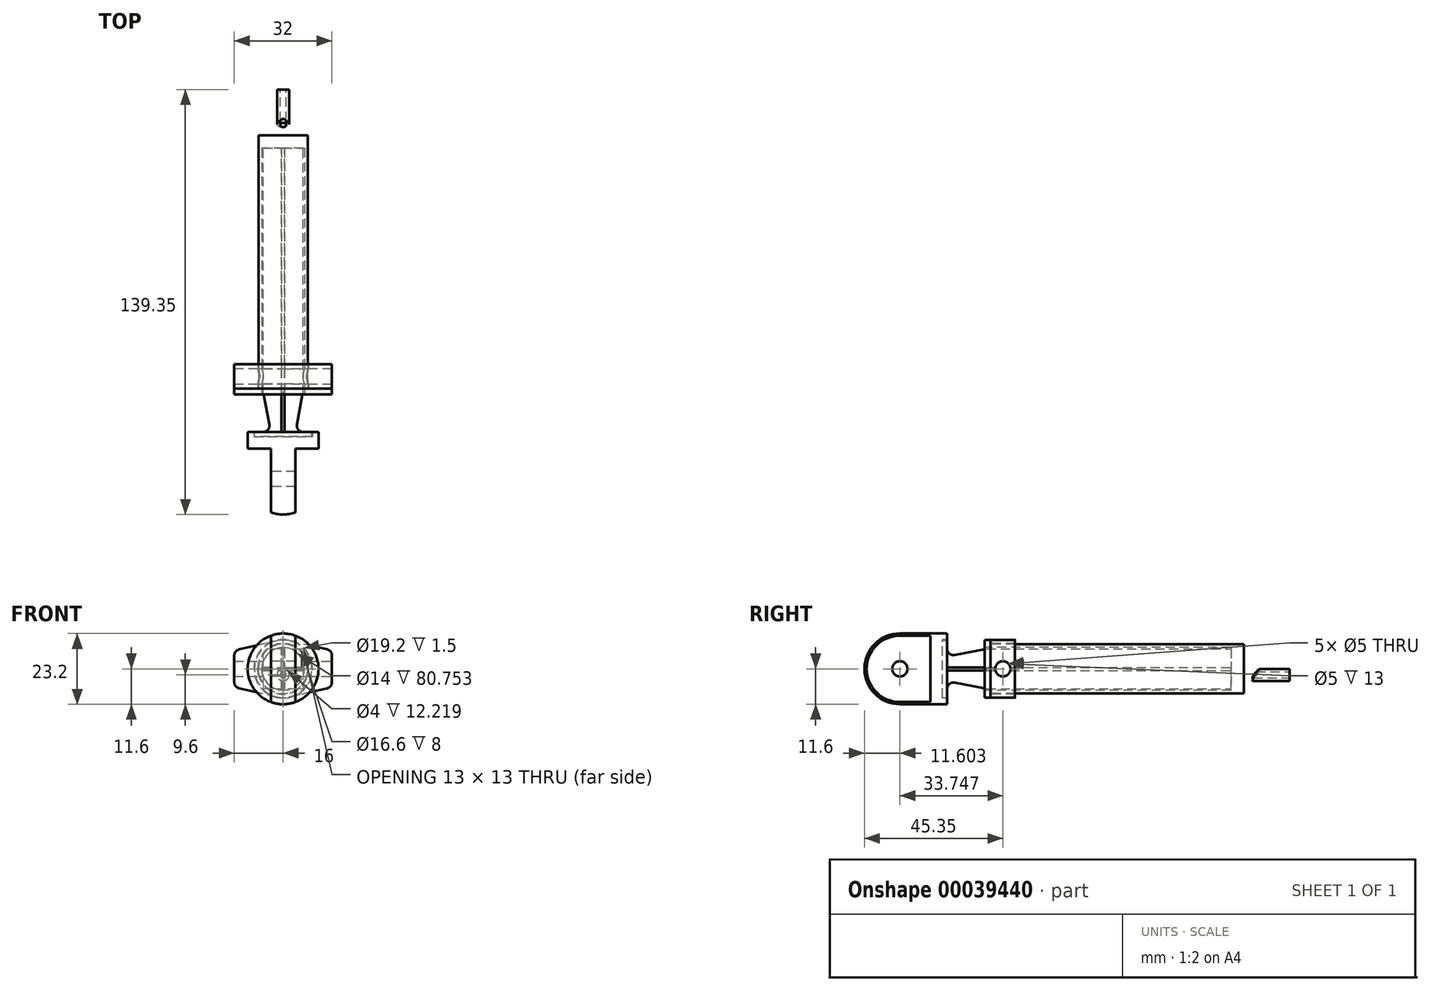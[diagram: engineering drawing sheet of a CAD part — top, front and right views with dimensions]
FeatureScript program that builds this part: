
annotation { "Feature Type Name" : "Feature", "Feature Type Description" : "" }
export const myFeature = defineFeature(function(context is Context, id is Id, definition is map)
    precondition{}
    {
        {
            var Q0;
            Q0=qCreatedBy(makeId("Front.planeOp"),FACE);
            var sketch = newSketch(context, id + "F0", { "sketchPlane" : qUnion([Q0])});
            skCircle(sketch, "E0", {"center": v(0, 0) * mm, "radius": 7 * mm});
            skArc(sketch, "E1", {"start": v(-2.17, -9.25) * mm, "mid": v(0, -9.5) * mm, "end": v(2.17, -9.25) * mm});
            skLineSegment(sketch, "E2", {"start": v(-2.17, -9.25) * mm, "end": v(-14.46, -6.36) * mm});
            skLineSegment(sketch, "E3", {"start": v(-16, -4.42) * mm, "end": v(-16, 4.42) * mm});
            skLineSegment(sketch, "E4", {"start": v(-14.46, 6.36) * mm, "end": v(-2.17, 9.25) * mm});
            skLineSegment(sketch, "E5", {"start": v(2.17, 9.25) * mm, "end": v(14.46, 6.36) * mm});
            skLineSegment(sketch, "E6", {"start": v(16, 4.42) * mm, "end": v(16, -4.42) * mm});
            skLineSegment(sketch, "E7", {"start": v(14.46, -6.36) * mm, "end": v(2.17, -9.25) * mm});
            skLineSegment(sketch, "E8", {"start": v(-16, 0) * mm, "end": v(16, 0) * mm, "construction": true});
            skArc(sketch, "E9.trimOffspring", {"start": v(2.17, 9.25) * mm, "mid": v(0, 9.5) * mm, "end": v(-2.17, 9.25) * mm});
            skPoint(sketch, "E10.visualSharp", {"position": v(-16, 6) * mm});
            skArc(sketch, "E10.filletArc", {"start": v(-14.46, 6.36) * mm, "mid": v(-15.57, 5.66) * mm, "end": v(-16, 4.42) * mm});
            skPoint(sketch, "E11.visualSharp", {"position": v(-16, -6) * mm});
            skArc(sketch, "E11.filletArc", {"start": v(-16, -4.42) * mm, "mid": v(-15.57, -5.66) * mm, "end": v(-14.46, -6.36) * mm});
            skPoint(sketch, "E12.visualSharp", {"position": v(16, -6) * mm});
            skArc(sketch, "E12.filletArc", {"start": v(14.46, -6.36) * mm, "mid": v(15.57, -5.66) * mm, "end": v(16, -4.42) * mm});
            skPoint(sketch, "E13.visualSharp", {"position": v(16, 6) * mm});
            skArc(sketch, "E13.filletArc", {"start": v(16, 4.42) * mm, "mid": v(15.57, 5.66) * mm, "end": v(14.46, 6.36) * mm});
            skSolve(sketch);
        }
        {
            var Q0;
            Q0=makeQuery(id+"F0.imprint","IMPRINT",FACE,{"disambiguationData":[TD([[makeQuery(id+"F0.imprint","IMPRINT",EDGE,{"derivedFrom":sQuery(id+"F0.wireOp",EDGE,"E0")}),-1.0]])]});
            extrude(context, id + "F1", {"entities" : qUnion([Q0]), "oppositeDirection" : true, "depth" : 2 * mm});
        }
        {
            var Q0;
            Q0=makeQuery(id+"F1.opExtrude","CAP_FACE",FACE,{"disambiguationData":[OSD([sQuery(id+"F0.wireOp",EDGE,"E0"),sQuery(id+"F0.wireOp",EDGE,"E1"),sQuery(id+"F0.wireOp",EDGE,"E2"),sQuery(id+"F0.wireOp",EDGE,"E3"),sQuery(id+"F0.wireOp",EDGE,"E4"),sQuery(id+"F0.wireOp",EDGE,"E5"),sQuery(id+"F0.wireOp",EDGE,"E6"),sQuery(id+"F0.wireOp",EDGE,"E7"),sQuery(id+"F0.wireOp",EDGE,"E9.trimOffspring"),sQuery(id+"F0.wireOp",EDGE,"E10.filletArc"),sQuery(id+"F0.wireOp",EDGE,"E11.filletArc"),sQuery(id+"F0.wireOp",EDGE,"E12.filletArc"),sQuery(id+"F0.wireOp",EDGE,"E13.filletArc")])],"isStart":false});
            var sketch = newSketch(context, id + "F2", { "sketchPlane" : qUnion([Q0])});
            skCircle(sketch, "E14.0", {"center": v(0, 0) * mm, "radius": 7 * mm});
            skCircle(sketch, "E15", {"center": v(0, 0) * mm, "radius": 8.1 * mm});
            skSolve(sketch);
        }
        {
            var Q0;
            Q0=makeQuery(id+"F2.imprint","IMPRINT",FACE,{"disambiguationData":[TD([[makeQuery(id+"F2.imprint","IMPRINT",EDGE,{"derivedFrom":sQuery(id+"F2.wireOp",EDGE,"E14.0")}),1.0]])]});
            extrude(context, id + "F3", {"entities" : qUnion([Q0]), "operationType" : NewBodyOperationType.ADD, "depth" : 83 * mm});
        }
        {
            var Q0;
            Q0=qCreatedBy(makeId("Right.planeOp"),FACE);
            var sketch = newSketch(context, id + "F4", { "sketchPlane" : qUnion([Q0])});
            skLineSegment(sketch, "E16", {"start": v(85, 0) * mm, "end": v(90.5, 0) * mm, "construction": true});
            skLineSegment(sketch, "E17", {"start": v(90.5, 0) * mm, "end": v(85, 8.1) * mm});
            skLineSegment(sketch, "E18", {"start": v(85, 7) * mm, "end": v(89.75, 0) * mm});
            skLineSegment(sketch, "E19", {"start": v(85, 8.1) * mm, "end": v(85, 7) * mm});
            skLineSegment(sketch, "E20", {"start": v(85, 7) * mm, "end": v(85, -7) * mm, "construction": true});
            skLineSegment(sketch, "E21", {"start": v(89.75, 0) * mm, "end": v(90.5, 0) * mm});
            skSolve(sketch);
        }
        {
            var Q0;
            Q0=makeQuery(id+"F4.imprint","IMPRINT",FACE,{"disambiguationData":[TD([[makeQuery(id+"F4.imprint","IMPRINT",EDGE,{"derivedFrom":sQuery(id+"F4.wireOp",EDGE,"E17")}),1.0]])]});
            var Q1;
            Q1=sQuery(id+"F4.wireOp",EDGE,"E17");
            var Q2;
            Q2=sQuery(id+"F4.wireOp",EDGE,"E21");
            var Q3;
            Q3=sQuery(id+"F4.wireOp",EDGE,"E18");
            var Q4;
            Q4=sQuery(id+"F4.wireOp",EDGE,"E19");
            var Q5;
            Q5=sQuery(id+"F4.wireOp",EDGE,"E16");
            revolve(context, id + "F5", {"operationType" : NewBodyOperationType.ADD, "entities" : qUnion([Q0]), "surfaceEntities" : qUnion([Q1, Q2, Q3, Q4]), "axis" : qUnion([Q5]), "revolveType" : RevolveType.FULL});
        }
        {
            var Q0;
            Q0=qCreatedBy(makeId("Front.planeOp"),FACE);
            cPlane(context, id + "F6", {"entities" : qUnion([Q0]), "cplaneType" : CPlaneType.OFFSET, "offset" : 100 * mm, "oppositeDirection" : true, "width" : 150 * mm, "height" : 150 * mm});
        }
        {
            var Q0;
            Q0=qCreatedBy(id+"F6.planeOp",FACE);
            var sketch = newSketch(context, id + "F7", { "sketchPlane" : qUnion([Q0])});
            skCircle(sketch, "E22.0", {"center": v(0, 0) * mm, "radius": 8.1 * mm, "construction": true});
            skCircle(sketch, "E23", {"center": v(0, -2) * mm, "radius": 2 * mm});
            skSolve(sketch);
        }
        {
            var Q0;
            Q0=makeQuery(id+"F7.imprint","IMPRINT",FACE,{"disambiguationData":[TD([[makeQuery(id+"F7.imprint","IMPRINT",EDGE,{"derivedFrom":sQuery(id+"F7.wireOp",EDGE,"E23")}),1.0]])]});
            extrude(context, id + "F8", {"entities" : qUnion([Q0]), "operationType" : NewBodyOperationType.ADD, "endBound" : BoundingType.UP_TO_NEXT, "depth" : 25 * mm});
        }
        {
            var Q0;
            Q0=makeQuery(id+"F8.opExtrude","CAP_FACE",FACE,{"disambiguationData":[OSD([sQuery(id+"F7.wireOp",EDGE,"E23")])],"isStart":true});
            var sketch = newSketch(context, id + "F9", { "sketchPlane" : qUnion([Q0])});
            skCircle(sketch, "E24", {"center": v(0, -2) * mm, "radius": 1 * mm});
            skSolve(sketch);
        }
        {
            var Q0;
            Q0=makeQuery(id+"F9.imprint","IMPRINT",FACE,{"disambiguationData":[TD([[makeQuery(id+"F9.imprint","IMPRINT",EDGE,{"derivedFrom":sQuery(id+"F9.wireOp",EDGE,"E24")}),1.0]])]});
            extrude(context, id + "F10", {"entities" : qUnion([Q0]), "operationType" : NewBodyOperationType.REMOVE, "endBound" : BoundingType.UP_TO_NEXT, "oppositeDirection" : true, "depth" : 25 * mm});
        }
        {
            var Q0;
            Q0=qCreatedBy(makeId("Right.planeOp"),FACE);
            var sketch = newSketch(context, id + "F11", { "sketchPlane" : qUnion([Q0])});
            skLineSegment(sketch, "E25.0", {"start": v(85, -7) * mm, "end": v(85, 7) * mm, "construction": true});
            skLineSegment(sketch, "E26", {"start": v(85, 7) * mm, "end": v(89.75, 0) * mm, "construction": true});
            skLineSegment(sketch, "E27", {"start": v(89.75, 0) * mm, "end": v(85, 7) * mm});
            skLineSegment(sketch, "E28", {"start": v(85, 7) * mm, "end": v(80.75, 7) * mm});
            skLineSegment(sketch, "E29", {"start": v(80.75, 7) * mm, "end": v(80.75, 0) * mm});
            skLineSegment(sketch, "E30", {"start": v(80.75, 0) * mm, "end": v(89.75, 0) * mm});
            skSolve(sketch);
        }
        {
            var Q0;
            Q0=makeQuery(id+"F11.imprint","IMPRINT",FACE,{"disambiguationData":[TD([[makeQuery(id+"F11.imprint","IMPRINT",EDGE,{"derivedFrom":sQuery(id+"F11.wireOp",EDGE,"E27")}),1.0]])]});
            var Q1;
            Q1=sQuery(id+"F11.wireOp",EDGE,"E30");
            revolve(context, id + "F12", {"entities" : qUnion([Q0]), "axis" : qUnion([Q1]), "revolveType" : RevolveType.FULL});
        }
        {
            var Q0;
            Q0=qCreatedBy(makeId("Right.planeOp"),FACE);
            var sketch = newSketch(context, id + "F13", { "sketchPlane" : qUnion([Q0])});
            skLineSegment(sketch, "E31.0.0", {"start": v(80.75, -7) * mm, "end": v(80.75, 7) * mm, "construction": true});
            skLineSegment(sketch, "E32", {"start": v(80.75, 0) * mm, "end": v(-12.25, 0) * mm});
            skLineSegment(sketch, "E33", {"start": v(-12.25, 0) * mm, "end": v(-12.25, 6.5) * mm});
            skArc(sketch, "E34", {"start": v(-12.25, 6.5) * mm, "mid": v(-11.53, 4.96) * mm, "end": v(-9.88, 4.53) * mm});
            skLineSegment(sketch, "E35", {"start": v(-9.88, 4.53) * mm, "end": v(0.75, 6.5) * mm});
            skLineSegment(sketch, "E36", {"start": v(0.75, 6.5) * mm, "end": v(80.75, 6.5) * mm});
            skLineSegment(sketch, "E37", {"start": v(80.75, 6.5) * mm, "end": v(80.75, 0) * mm});
            skSolve(sketch);
        }
        {
            var Q0;
            Q0=makeQuery(id+"F13.imprint","IMPRINT",FACE,{"disambiguationData":[TD([[makeQuery(id+"F13.imprint","IMPRINT",EDGE,{"derivedFrom":sQuery(id+"F13.wireOp",EDGE,"E32")}),-1.0]])]});
            extrude(context, id + "F14", {"entities" : qUnion([Q0]), "operationType" : NewBodyOperationType.ADD, "endBound" : BoundingType.SYMMETRIC, "depth" : 1 * mm});
        }
        {
            var Q0;
            Q0=makeQuery(id+"F12.opRevolve","SWEPT_BODY",BODY,{"disambiguationData":[OSD([sQuery(id+"F11.wireOp",EDGE,"E27"),sQuery(id+"F11.wireOp",EDGE,"E28"),sQuery(id+"F11.wireOp",EDGE,"E29"),sQuery(id+"F11.wireOp",EDGE,"E30")])]});
            var Q1;
            Q1=makeQuery(id+"F1.opExtrude","CAP_EDGE",EDGE,{"disambiguationData":[OSD([sQuery(id+"F0.wireOp",EDGE,"E0")])],"isStart":true});
            circularPattern(context, id + "F15", {"operationType" : NewBodyOperationType.ADD, "entities" : qUnion([Q0]), "axis" : qUnion([Q1]), "angle" : 360 * degree, "instanceCount" : 4, "equalSpace" : true});
        }
        {
            var Q0;
            {var subQ0=makeQuery(id+"F14.opExtrude","SWEPT_FACE",FACE,{"disambiguationData":[OSD([sQuery(id+"F13.wireOp",EDGE,"E33")])]});Q0=makeQuery(id+"F15.boolean.opBoolean","MERGE",FACE,{"derivedFrom":[subQ0,makeQuery(id+"F15.opPattern","COPY",FACE,{"derivedFrom":subQ0,"instanceName":"1"}),makeQuery(id+"F15.opPattern","COPY",FACE,{"derivedFrom":subQ0,"instanceName":"2"}),makeQuery(id+"F15.opPattern","COPY",FACE,{"derivedFrom":subQ0,"instanceName":"3"})]});}
            var sketch = newSketch(context, id + "F16", { "sketchPlane" : qUnion([Q0])});
            skCircle(sketch, "E38", {"center": v(0, 0) * mm, "radius": 9.4 * mm});
            skSolve(sketch);
        }
        {
            var Q0;
            Q0=makeQuery(id+"F16.imprint","IMPRINT",FACE,{"disambiguationData":[TD([[makeQuery(id+"F16.imprint","IMPRINT",EDGE,{"derivedFrom":sQuery(id+"F16.wireOp",EDGE,"E38")}),1.0]])]});
            var Q1;
            {var subQ0=sQuery(id+"F13.wireOp",EDGE,"E33");var subQ3=makeQuery(id+"F14.opExtrude","CAP_EDGE",EDGE,{"disambiguationData":[OSD([subQ0])],"isStart":true});Q1=makeQuery(id+"F16.imprint","IMPRINT",FACE,{"disambiguationData":[TD([[makeQuery(id+"F16.imprint","IMPRINT",EDGE,{"derivedFrom":subQ3}),-1.0]])]});}
            extrude(context, id + "F17", {"entities" : qUnion([Q0, Q1]), "operationType" : NewBodyOperationType.ADD, "depth" : 1.5 * mm});
        }
        {
            var Q0;
            Q0=makeQuery(id+"F1.opExtrude","CAP_FACE",FACE,{"disambiguationData":[OSD([sQuery(id+"F0.wireOp",EDGE,"E0"),sQuery(id+"F0.wireOp",EDGE,"E1"),sQuery(id+"F0.wireOp",EDGE,"E2"),sQuery(id+"F0.wireOp",EDGE,"E3"),sQuery(id+"F0.wireOp",EDGE,"E4"),sQuery(id+"F0.wireOp",EDGE,"E5"),sQuery(id+"F0.wireOp",EDGE,"E6"),sQuery(id+"F0.wireOp",EDGE,"E7"),sQuery(id+"F0.wireOp",EDGE,"E9.trimOffspring"),sQuery(id+"F0.wireOp",EDGE,"E10.filletArc"),sQuery(id+"F0.wireOp",EDGE,"E11.filletArc"),sQuery(id+"F0.wireOp",EDGE,"E12.filletArc"),sQuery(id+"F0.wireOp",EDGE,"E13.filletArc")])],"isStart":false});
            cPlane(context, id + "F18", {"entities" : qUnion([Q0]), "cplaneType" : CPlaneType.OFFSET, "offset" : 0 * mm, "width" : 150 * mm, "height" : 150 * mm});
        }
        {
            var Q0;
            Q0=qCreatedBy(id+"F18.planeOp",FACE);
            var sketch = newSketch(context, id + "F19", { "sketchPlane" : qUnion([Q0])});
            skLineSegment(sketch, "E39.0.0", {"start": v(2.17, -9.25) * mm, "end": v(14.46, -6.36) * mm});
            skArc(sketch, "E39.0.1", {"start": v(14.46, -6.36) * mm, "mid": v(15.57, -5.66) * mm, "end": v(16, -4.42) * mm});
            skLineSegment(sketch, "E39.0.2", {"start": v(16, -4.42) * mm, "end": v(16, 4.42) * mm});
            skArc(sketch, "E39.0.3", {"start": v(16, 4.42) * mm, "mid": v(15.57, 5.66) * mm, "end": v(14.46, 6.36) * mm});
            skLineSegment(sketch, "E39.0.4", {"start": v(14.46, 6.36) * mm, "end": v(2.17, 9.25) * mm});
            skArc(sketch, "E39.0.5", {"start": v(2.17, 9.25) * mm, "mid": v(0, 9.5) * mm, "end": v(-2.17, 9.25) * mm});
            skLineSegment(sketch, "E39.0.6", {"start": v(-2.17, 9.25) * mm, "end": v(-14.46, 6.36) * mm});
            skArc(sketch, "E39.0.7", {"start": v(-14.46, 6.36) * mm, "mid": v(-15.57, 5.66) * mm, "end": v(-16, 4.42) * mm});
            skLineSegment(sketch, "E39.0.8", {"start": v(-16, 4.42) * mm, "end": v(-16, -4.42) * mm});
            skArc(sketch, "E39.0.9", {"start": v(-16, -4.42) * mm, "mid": v(-15.57, -5.66) * mm, "end": v(-14.46, -6.36) * mm});
            skLineSegment(sketch, "E39.0.10", {"start": v(-14.46, -6.36) * mm, "end": v(-2.17, -9.25) * mm});
            skArc(sketch, "E39.0.11", {"start": v(-2.17, -9.25) * mm, "mid": v(0, -9.5) * mm, "end": v(2.17, -9.25) * mm});
            skCircle(sketch, "E40", {"center": v(0, 0) * mm, "radius": 8.3 * mm});
            skSolve(sketch);
        }
        {
            var Q0;
            Q0=makeQuery(id+"F19.imprint","IMPRINT",FACE,{"disambiguationData":[TD([[makeQuery(id+"F19.imprint","IMPRINT",EDGE,{"derivedFrom":sQuery(id+"F19.wireOp",EDGE,"E39.0.0")}),1.0]])]});
            extrude(context, id + "F20", {"entities" : qUnion([Q0]), "depth" : 8 * mm});
        }
        {
            var Q0;
            Q0=makeQuery(id+"F20.opExtrude","SWEPT_FACE",FACE,{"disambiguationData":[OSD([sQuery(id+"F19.wireOp",EDGE,"E39.0.8")])]});
            var sketch = newSketch(context, id + "F21", { "sketchPlane" : qUnion([Q0])});
            skLineSegment(sketch, "E41", {"start": v(2, 4.42) * mm, "end": v(10, -4.42) * mm, "construction": true});
            skCircle(sketch, "E42", {"center": v(6, 0) * mm, "radius": 2.5 * mm});
            skSolve(sketch);
        }
        {
            var Q0;
            Q0=makeQuery(id+"F21.imprint","IMPRINT",FACE,{"disambiguationData":[TD([[makeQuery(id+"F21.imprint","IMPRINT",EDGE,{"derivedFrom":sQuery(id+"F21.wireOp",EDGE,"E42")}),1.0]])]});
            extrude(context, id + "F22", {"entities" : qUnion([Q0]), "operationType" : NewBodyOperationType.REMOVE, "endBound" : BoundingType.THROUGH_ALL, "oppositeDirection" : true, "depth" : 25 * mm});
        }
        {
            var Q0;
            Q0=qCreatedBy(makeId("Right.planeOp"),FACE);
            var sketch = newSketch(context, id + "F23", { "sketchPlane" : qUnion([Q0])});
            skLineSegment(sketch, "E43", {"start": v(-13.75, 0) * mm, "end": v(-13.75, 9.6) * mm});
            skLineSegment(sketch, "E44", {"start": v(-12.25, 9.6) * mm, "end": v(-13.75, 9.6) * mm});
            skLineSegment(sketch, "E45.0", {"start": v(-12.25, -9.4) * mm, "end": v(-12.25, 9.4) * mm});
            skLineSegment(sketch, "E46", {"start": v(-12.25, 9.6) * mm, "end": v(-12.25, 11.6) * mm});
            skLineSegment(sketch, "E47", {"start": v(-12.25, 11.6) * mm, "end": v(-17.75, 11.6) * mm});
            skLineSegment(sketch, "E48", {"start": v(-17.75, 11.6) * mm, "end": v(-17.75, 0) * mm});
            skLineSegment(sketch, "E49", {"start": v(-17.75, 0) * mm, "end": v(-13.75, 0) * mm});
            skLineSegment(sketch, "E50.0", {"start": v(-13.75, -9.4) * mm, "end": v(-13.75, 9.4) * mm});
            skSolve(sketch);
        }
        {
            var Q0;
            {var subQ1=sQuery(id+"F23.wireOp",EDGE,"E43");Q0=makeQuery(id+"F23.imprint","IMPRINT",FACE,{"disambiguationData":[TD([[makeQuery(id+"F23.imprint","IMPRINT",EDGE,{"derivedFrom":subQ1}),1.0]])]});}
            var Q1;
            Q1=sQuery(id+"F23.wireOp",EDGE,"E49");
            revolve(context, id + "F24", {"entities" : qUnion([Q0]), "axis" : qUnion([Q1]), "revolveType" : RevolveType.FULL});
        }
        {
            var Q0;
            Q0=makeQuery(id+"F24.opRevolve","SWEPT_FACE",FACE,{"disambiguationData":[OSD([sQuery(id+"F23.wireOp",EDGE,"E48")])]});
            var sketch = newSketch(context, id + "F25", { "sketchPlane" : qUnion([Q0])});
            skLineSegment(sketch, "E51", {"start": v(-4, 0) * mm, "end": v(4, 0) * mm});
            skLineSegment(sketch, "E52", {"start": v(4, 0) * mm, "end": v(4, 10.89) * mm});
            skLineSegment(sketch, "E53", {"start": v(-4, 0) * mm, "end": v(-4, 10.89) * mm});
            skArc(sketch, "E54", {"start": v(4, 10.89) * mm, "mid": v(0, 11.6) * mm, "end": v(-4, 10.89) * mm});
            skLineSegment(sketch, "E55.MirrorCS", {"start": v(-4, 0) * mm, "end": v(-4, -10.89) * mm});
            skLineSegment(sketch, "E56.MirrorCS", {"start": v(4, 0) * mm, "end": v(4, -10.89) * mm});
            skArc(sketch, "E57.MirrorCS", {"start": v(4, -10.89) * mm, "mid": v(0, -11.6) * mm, "end": v(-4, -10.89) * mm});
            skSolve(sketch);
        }
        {
            var Q0;
            Q0 = qSketchRegion(id + "F25", true);
            extrude(context, id + "F26", {"entities" : qUnion([Q0]), "operationType" : NewBodyOperationType.ADD, "depth" : 10 * mm});
        }
        {
            var Q0;
            Q0=makeQuery(id+"F26.opExtrude","CAP_FACE",FACE,{"disambiguationData":[OSD([sQuery(id+"F25.wireOp",EDGE,"E52"),sQuery(id+"F25.wireOp",EDGE,"E53"),sQuery(id+"F25.wireOp",EDGE,"E54"),sQuery(id+"F25.wireOp",EDGE,"E55.MirrorCS"),sQuery(id+"F25.wireOp",EDGE,"E56.MirrorCS"),sQuery(id+"F25.wireOp",EDGE,"E57.MirrorCS")])],"isStart":false});
            var sketch = newSketch(context, id + "F27", { "sketchPlane" : qUnion([Q0])});
            skArc(sketch, "E58.0", {"start": v(4, 10.89) * mm, "mid": v(0, 11.6) * mm, "end": v(-4, 10.89) * mm});
            skLineSegment(sketch, "E58.1", {"start": v(-4, -10.89) * mm, "end": v(-4, 10.89) * mm});
            skLineSegment(sketch, "E58.2", {"start": v(4, -10.89) * mm, "end": v(4, 10.89) * mm});
            skArc(sketch, "E58.3", {"start": v(-4, -10.89) * mm, "mid": v(0, -11.6) * mm, "end": v(4, -10.89) * mm});
            skLineSegment(sketch, "E59", {"start": v(-4, 0) * mm, "end": v(4, 0) * mm});
            skSolve(sketch);
        }
        {
            var Q0;
            {var subQ2=sQuery(id+"F27.wireOp",EDGE,"E58.0");Q0=makeQuery(id+"F27.imprint","IMPRINT",FACE,{"disambiguationData":[TD([[makeQuery(id+"F27.imprint","IMPRINT",EDGE,{"derivedFrom":subQ2}),1.0]])]});}
            var Q1;
            Q1=sQuery(id+"F27.wireOp",EDGE,"E59");
            revolve(context, id + "F28", {"operationType" : NewBodyOperationType.ADD, "entities" : qUnion([Q0]), "axis" : qUnion([Q1]), "revolveType" : RevolveType.FULL});
        }
        {
            var Q0;
            Q0=makeQuery(id+"F28.boolean.opBoolean","MERGE",FACE,{"derivedFrom":[makeQuery(id+"F26.opExtrude","SWEPT_FACE",FACE,{"disambiguationData":[OSD([sQuery(id+"F25.wireOp",EDGE,"E53"),sQuery(id+"F25.wireOp",EDGE,"E55.MirrorCS")])]}),makeQuery(id+"F28.opRevolve","SWEPT_FACE",FACE,{"disambiguationData":[OSD([sQuery(id+"F27.wireOp",EDGE,"E58.1")])]})]});
            var sketch = newSketch(context, id + "F29", { "sketchPlane" : qUnion([Q0])});
            skCircle(sketch, "E60", {"center": v(27.75, 0) * mm, "radius": 2.5 * mm});
            skSolve(sketch);
        }
        {
            var Q0;
            Q0=makeQuery(id+"F29.imprint","IMPRINT",FACE,{"disambiguationData":[TD([[makeQuery(id+"F29.imprint","IMPRINT",EDGE,{"derivedFrom":sQuery(id+"F29.wireOp",EDGE,"E60")}),1.0]])]});
            extrude(context, id + "F30", {"entities" : qUnion([Q0]), "operationType" : NewBodyOperationType.REMOVE, "endBound" : BoundingType.THROUGH_ALL, "oppositeDirection" : true, "depth" : 25 * mm});
        }
    });
